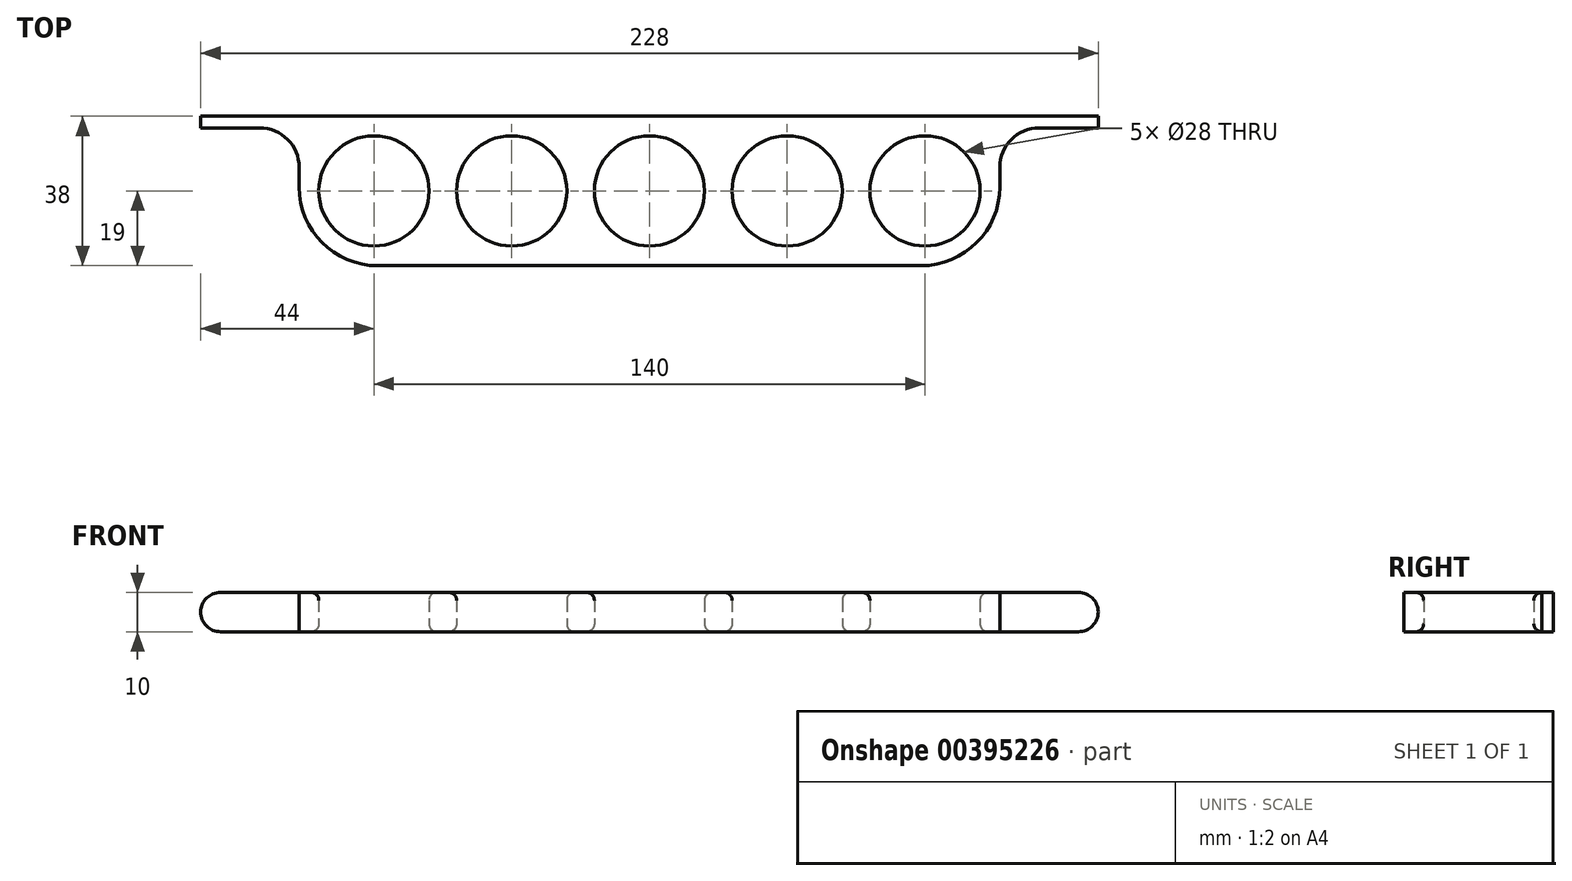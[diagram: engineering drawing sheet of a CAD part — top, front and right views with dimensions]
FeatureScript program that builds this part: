
annotation { "Feature Type Name" : "Feature", "Feature Type Description" : "" }
export const myFeature = defineFeature(function(context is Context, id is Id, definition is map)
    precondition{}
    {
        {
            var Q0;
            Q0=qCreatedBy(makeId("Top.planeOp"),FACE);
            var sketch = newSketch(context, id + "F0", { "sketchPlane" : qUnion([Q0])});
            skLineSegment(sketch, "E0.bottom", {"start": v(-89, 19) * mm, "end": v(89, 19) * mm});
            skLineSegment(sketch, "E0.top", {"start": v(-69, -19) * mm, "end": v(69, -19) * mm});
            skLineSegment(sketch, "E0.left", {"start": v(-89, 6) * mm, "end": v(-89, 1) * mm});
            skLineSegment(sketch, "E0.right", {"start": v(89, 6) * mm, "end": v(89, 1) * mm});
            skPoint(sketch, "E0.middle", {"position": v(0, 0) * mm});
            skCircle(sketch, "E1", {"center": v(-70, 0) * mm, "radius": 14 * mm});
            skCircle(sketch, "E2.1.0.0", {"center": v(-35, 0) * mm, "radius": 14 * mm});
            skCircle(sketch, "E2.2.0.0", {"center": v(0, 0) * mm, "radius": 14 * mm});
            skCircle(sketch, "E2.3.0.0", {"center": v(35, 0) * mm, "radius": 14 * mm});
            skCircle(sketch, "E2.4.0.0", {"center": v(70, 0) * mm, "radius": 14 * mm});
            skLineSegment(sketch, "E2.direction1", {"start": v(-70, 0) * mm, "end": v(-35, 0) * mm, "construction": true});
            skLineSegment(sketch, "E3.bottom", {"start": v(-89, 19) * mm, "end": v(-114, 19) * mm});
            skLineSegment(sketch, "E3.top", {"start": v(-99, 16) * mm, "end": v(-114, 16) * mm});
            skLineSegment(sketch, "E3.left", {"start": v(-89, 19) * mm, "end": v(-89, 17) * mm});
            skLineSegment(sketch, "E3.right", {"start": v(-114, 19) * mm, "end": v(-114, 16) * mm});
            skLineSegment(sketch, "E4.bottom", {"start": v(89, 19) * mm, "end": v(114, 19) * mm});
            skLineSegment(sketch, "E4.top", {"start": v(99, 16) * mm, "end": v(114, 16) * mm});
            skLineSegment(sketch, "E4.left", {"start": v(89, 19) * mm, "end": v(89, 17) * mm});
            skLineSegment(sketch, "E4.right", {"start": v(114, 19) * mm, "end": v(114, 16) * mm});
            skArc(sketch, "E5.filletArc", {"start": v(99, 16) * mm, "mid": v(91.93, 13.07) * mm, "end": v(89, 6) * mm});
            skArc(sketch, "E6.filletArc", {"start": v(-89, 6) * mm, "mid": v(-91.93, 13.07) * mm, "end": v(-99, 16) * mm});
            skPoint(sketch, "E7.visualSharp", {"position": v(-89, -19) * mm});
            skArc(sketch, "E7.filletArc", {"start": v(-89, 1) * mm, "mid": v(-83.14, -13.14) * mm, "end": v(-69, -19) * mm});
            skPoint(sketch, "E8.visualSharp", {"position": v(89, -19) * mm});
            skArc(sketch, "E8.filletArc", {"start": v(69, -19) * mm, "mid": v(83.14, -13.14) * mm, "end": v(89, 1) * mm});
            skSolve(sketch);
        }
        {
            var Q0;
            Q0=makeQuery(id+"F0.imprint","IMPRINT",FACE,{"disambiguationData":[TD([[makeQuery(id+"F0.imprint","IMPRINT",EDGE,{"derivedFrom":sQuery(id+"F0.wireOp",EDGE,"E0.bottom")}),-1.0]])]});
            extrude(context, id + "F1", {"entities" : qUnion([Q0]), "depth" : 10 * mm});
        }
        {
            var Q0;
            Q0=makeQuery(id+"F1.opExtrude","CAP_EDGE",EDGE,{"disambiguationData":[OSD([sQuery(id+"F0.wireOp",EDGE,"E1")])],"isStart":false});
            var Q1;
            Q1=makeQuery(id+"F1.opExtrude","CAP_EDGE",EDGE,{"disambiguationData":[OSD([sQuery(id+"F0.wireOp",EDGE,"E2.1.0.0")])],"isStart":false});
            var Q2;
            Q2=makeQuery(id+"F1.opExtrude","CAP_EDGE",EDGE,{"disambiguationData":[OSD([sQuery(id+"F0.wireOp",EDGE,"E2.2.0.0")])],"isStart":false});
            var Q3;
            Q3=makeQuery(id+"F1.opExtrude","CAP_EDGE",EDGE,{"disambiguationData":[OSD([sQuery(id+"F0.wireOp",EDGE,"E2.3.0.0")])],"isStart":false});
            var Q4;
            Q4=makeQuery(id+"F1.opExtrude","CAP_EDGE",EDGE,{"disambiguationData":[OSD([sQuery(id+"F0.wireOp",EDGE,"E2.4.0.0")])],"isStart":false});
            fillet(context, id + "F2", {"entities" : qUnion([Q0, Q1, Q2, Q3, Q4]), "radius" : 2 * mm, "tangentPropagation" : true, "allowEdgeOverflow" : false});
        }
        {
            var Q0;
            Q0=makeQuery(id+"F1.opExtrude","CAP_EDGE",EDGE,{"disambiguationData":[OSD([sQuery(id+"F0.wireOp",EDGE,"E3.right")])],"isStart":false});
            var Q1;
            Q1=makeQuery(id+"F1.opExtrude","CAP_EDGE",EDGE,{"disambiguationData":[OSD([sQuery(id+"F0.wireOp",EDGE,"E3.right")])],"isStart":true});
            var Q2;
            Q2=makeQuery(id+"F1.opExtrude","CAP_EDGE",EDGE,{"disambiguationData":[OSD([sQuery(id+"F0.wireOp",EDGE,"E4.right")])],"isStart":false});
            var Q3;
            Q3=makeQuery(id+"F1.opExtrude","CAP_EDGE",EDGE,{"disambiguationData":[OSD([sQuery(id+"F0.wireOp",EDGE,"E4.right")])],"isStart":true});
            fillet(context, id + "F3", {"entities" : qUnion([Q0, Q1, Q2, Q3]), "radius" : 5 * mm, "tangentPropagation" : true, "allowEdgeOverflow" : false});
        }
        {
            var Q0;
            Q0=makeQuery(id+"F1.opExtrude","CAP_EDGE",EDGE,{"disambiguationData":[OSD([sQuery(id+"F0.wireOp",EDGE,"E2.4.0.0")])],"isStart":true});
            var Q1;
            Q1=makeQuery(id+"F1.opExtrude","CAP_EDGE",EDGE,{"disambiguationData":[OSD([sQuery(id+"F0.wireOp",EDGE,"E2.3.0.0")])],"isStart":true});
            var Q2;
            Q2=makeQuery(id+"F1.opExtrude","CAP_EDGE",EDGE,{"disambiguationData":[OSD([sQuery(id+"F0.wireOp",EDGE,"E2.2.0.0")])],"isStart":true});
            var Q3;
            Q3=makeQuery(id+"F1.opExtrude","CAP_EDGE",EDGE,{"disambiguationData":[OSD([sQuery(id+"F0.wireOp",EDGE,"E2.1.0.0")])],"isStart":true});
            var Q4;
            Q4=makeQuery(id+"F1.opExtrude","CAP_EDGE",EDGE,{"disambiguationData":[OSD([sQuery(id+"F0.wireOp",EDGE,"E1")])],"isStart":true});
            fillet(context, id + "F4", {"entities" : qUnion([Q0, Q1, Q2, Q3, Q4]), "radius" : 2 * mm, "tangentPropagation" : true, "allowEdgeOverflow" : false});
        }
    });
